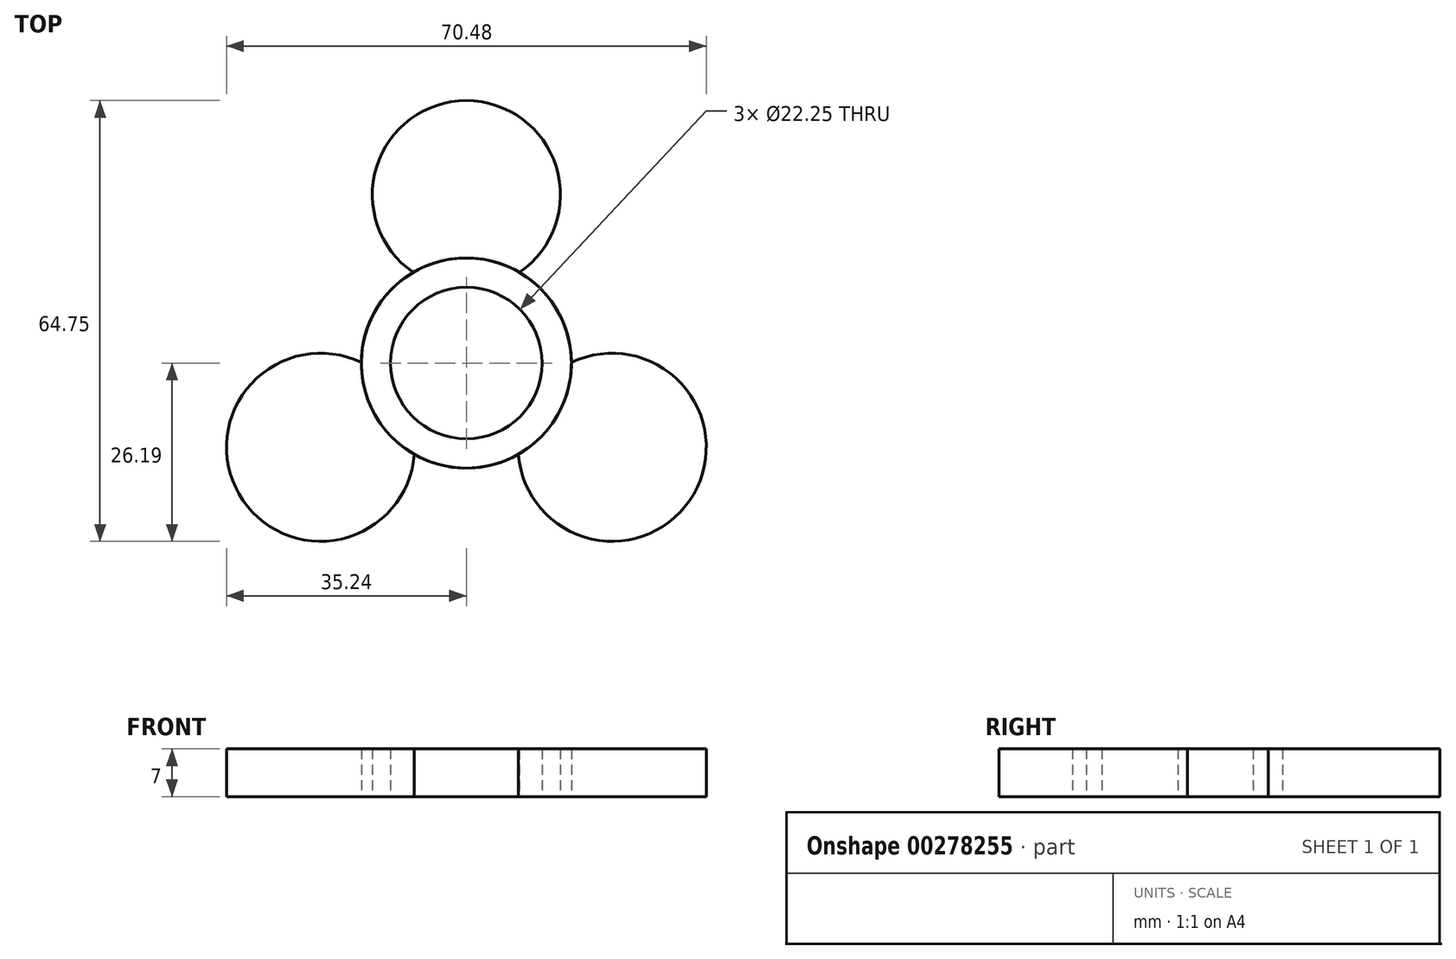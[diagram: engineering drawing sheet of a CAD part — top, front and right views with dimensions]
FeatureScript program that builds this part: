
annotation { "Feature Type Name" : "Feature", "Feature Type Description" : "" }
export const myFeature = defineFeature(function(context is Context, id is Id, definition is map)
    precondition{}
    {
        {
            var Q0;
            Q0=qCreatedBy(makeId("Top.planeOp"),FACE);
            var sketch = newSketch(context, id + "F0", { "sketchPlane" : qUnion([Q0])});
            skCircle(sketch, "E0", {"center": v(0, 0) * mm, "radius": 11.12 * mm});
            skCircle(sketch, "E1", {"center": v(0, 0) * mm, "radius": 15.44 * mm});
            skLineSegment(sketch, "E2", {"start": v(0, 0) * mm, "end": v(0, 38.56) * mm});
            skCircle(sketch, "E3", {"center": v(0, 24.74) * mm, "radius": 13.82 * mm});
            skLineSegment(sketch, "E4", {"start": v(0, 0) * mm, "end": v(-4.93, -1.19) * mm});
            skSolve(sketch);
        }
        {
            var Q0;
            Q0=sQuery(id+"F0.wireOp",EDGE,"E4");
            extrude(context, id + "F1", {"bodyType" : ExtendedToolBodyType.SURFACE, "surfaceEntities" : qUnion([Q0]), "depth" : 25 * mm, "offsetDistance" : 25 * mm});
        }
        {
            var Q0;
            {var subQ0=sQuery(id+"F0.wireOp",EDGE,"E3");var subQ1=sQuery(id+"F0.wireOp",EDGE,"E1");var subQ2=makeQuery(id+"F0.imprint","INTERSECT",VERTEX,{"disambiguationData":[OD(1.0)],"derivedFrom":[subQ1,subQ0]});Q0=makeQuery(id+"F0.imprint","IMPRINT",FACE,{"disambiguationData":[TD([[makeQuery(id+"F0.imprint","IMPRINT",EDGE,{"disambiguationData":[TD([[subQ2,1.0]])],"derivedFrom":subQ1}),-1.0]])]});}
            var Q1;
            {var subQ0=sQuery(id+"F0.wireOp",EDGE,"E3");var subQ1=sQuery(id+"F0.wireOp",EDGE,"E1");var subQ2=makeQuery(id+"F0.imprint","INTERSECT",VERTEX,{"disambiguationData":[OD(0.0)],"derivedFrom":[subQ1,subQ0]});Q1=makeQuery(id+"F0.imprint","IMPRINT",FACE,{"disambiguationData":[TD([[makeQuery(id+"F0.imprint","IMPRINT",EDGE,{"disambiguationData":[TD([[subQ2,-1.0]])],"derivedFrom":subQ1}),-1.0]])]});}
            var Q2;
            {var subQ0=sQuery(id+"F0.wireOp",EDGE,"E2");var subQ1=sQuery(id+"F0.wireOp",EDGE,"E0");var subQ2=makeQuery(id+"F0.imprint","INTERSECT",VERTEX,{"derivedFrom":[subQ1,subQ0]});Q2=makeQuery(id+"F0.imprint","IMPRINT",FACE,{"disambiguationData":[TD([[makeQuery(id+"F0.imprint","IMPRINT",EDGE,{"disambiguationData":[TD([[subQ2,-1.0]])],"derivedFrom":subQ1}),-1.0]])]});}
            var Q3;
            {var subQ0=sQuery(id+"F0.wireOp",EDGE,"E2");var subQ1=sQuery(id+"F0.wireOp",EDGE,"E0");var subQ2=makeQuery(id+"F0.imprint","INTERSECT",VERTEX,{"derivedFrom":[subQ1,subQ0]});Q3=makeQuery(id+"F0.imprint","IMPRINT",FACE,{"disambiguationData":[TD([[makeQuery(id+"F0.imprint","IMPRINT",EDGE,{"disambiguationData":[TD([[subQ2,1.0]])],"derivedFrom":subQ1}),-1.0]])]});}
            var Q4;
            {var subQ0=sQuery(id+"F0.wireOp",EDGE,"E3");var subQ1=sQuery(id+"F0.wireOp",EDGE,"E0");var subQ2=makeQuery(id+"F0.imprint","INTERSECT",VERTEX,{"disambiguationData":[OD(0.0)],"derivedFrom":[subQ1,subQ0]});Q4=makeQuery(id+"F0.imprint","IMPRINT",FACE,{"disambiguationData":[TD([[makeQuery(id+"F0.imprint","IMPRINT",EDGE,{"disambiguationData":[TD([[subQ2,1.0]])],"derivedFrom":subQ1}),-1.0]])]});}
            extrude(context, id + "F2", {"entities" : qUnion([Q0, Q1, Q2, Q3, Q4]), "depth" : 7 * mm, "offsetDistance" : 25 * mm});
        }
        {
            var Q0;
            Q0=makeQuery(id+"F2.opExtrude","SWEPT_BODY",BODY,{"disambiguationData":[OSD([sQuery(id+"F0.wireOp",EDGE,"E0"),sQuery(id+"F0.wireOp",EDGE,"E1"),sQuery(id+"F0.wireOp",EDGE,"E3")])]});
            var Q1;
            Q1=makeQuery(id+"F1.opExtrude","SWEPT_EDGE",EDGE,{"disambiguationData":[OSD([sQuery(id+"F0.wireOp",VERTEX,"E4.start")])]});
            circularPattern(context, id + "F3", {"entities" : qUnion([Q0]), "axis" : qUnion([Q1]), "angle" : 360 * degree, "instanceCount" : 3, "equalSpace" : true, "computeTransformsWithoutBuiltin" : true});
        }
    });
